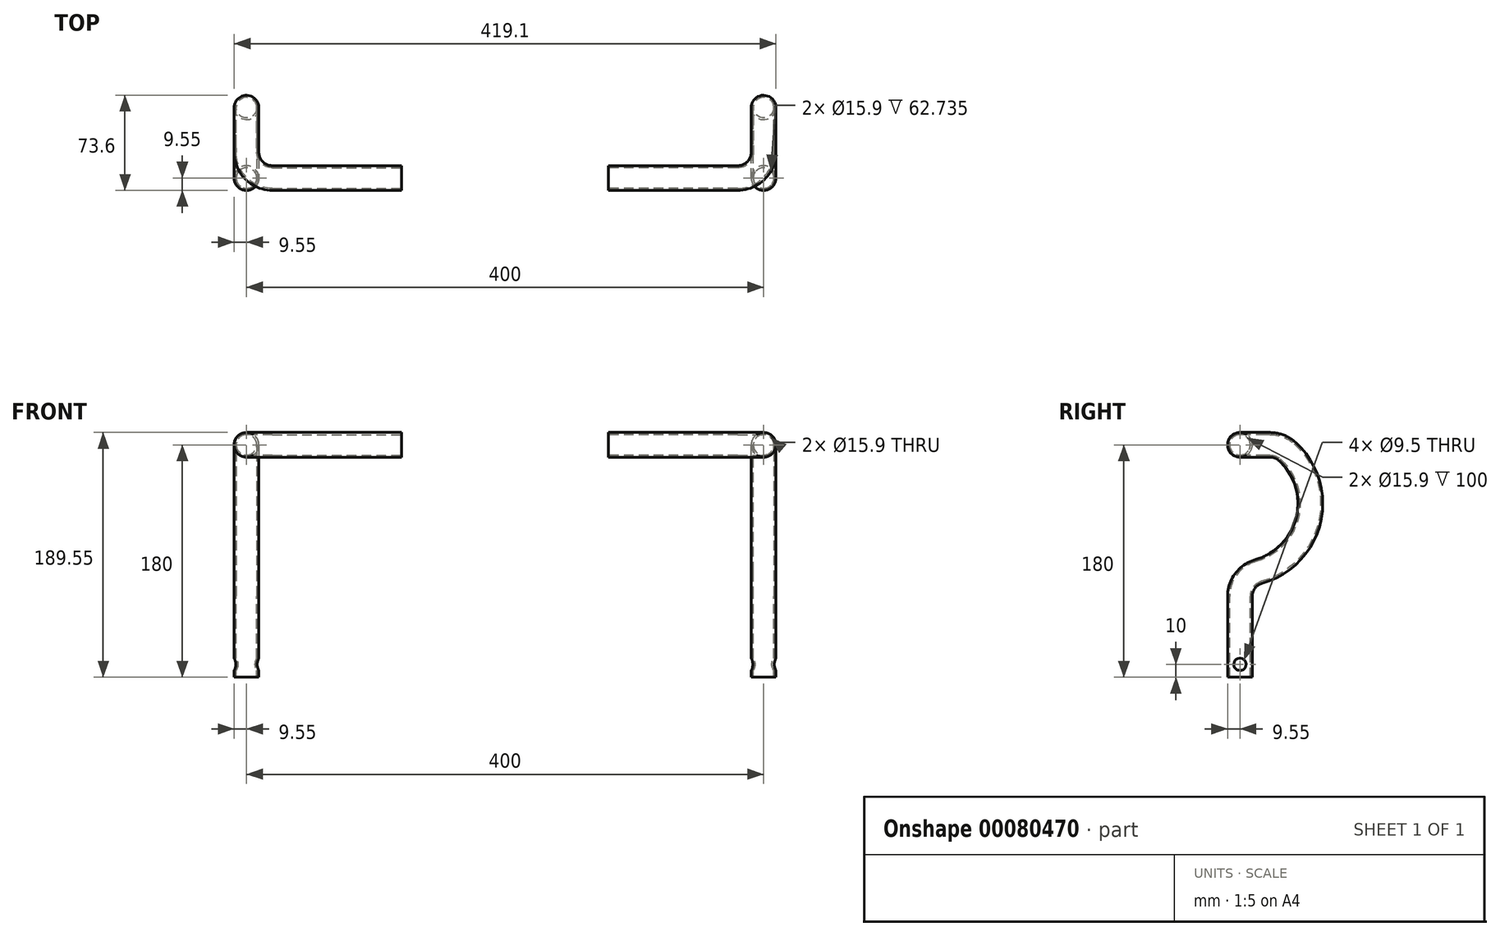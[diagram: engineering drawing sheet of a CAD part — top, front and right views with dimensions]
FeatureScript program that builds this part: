
annotation { "Feature Type Name" : "Feature", "Feature Type Description" : "" }
export const myFeature = defineFeature(function(context is Context, id is Id, definition is map)
    precondition{}
    {
        {
            var Q0;
            Q0=qCreatedBy(makeId("Right.planeOp"),FACE);
            var sketch = newSketch(context, id + "F0", { "sketchPlane" : qUnion([Q0])});
            skLineSegment(sketch, "E0", {"start": v(0, -117.27) * mm, "end": v(0, -180) * mm});
            skLineSegment(sketch, "E1", {"start": v(0, 0) * mm, "end": v(23.24, 0) * mm});
            skArc(sketch, "E2", {"start": v(14.63, -98) * mm, "mid": v(53.02, -58.12) * mm, "end": v(36.7, -5.22) * mm});
            skPoint(sketch, "E3.visualSharp", {"position": v(30, 0) * mm});
            skArc(sketch, "E3.filletArc", {"start": v(36.7, -5.22) * mm, "mid": v(30.46, -1.35) * mm, "end": v(23.24, 0) * mm});
            skPoint(sketch, "E4.visualSharp", {"position": v(0, -100) * mm});
            skArc(sketch, "E4.filletArc", {"start": v(14.63, -98) * mm, "mid": v(4.07, -105.17) * mm, "end": v(0, -117.27) * mm});
            skSolve(sketch);
        }
        {
            var Q0;
            Q0=qCreatedBy(makeId("Top.planeOp"),FACE);
            var sketch = newSketch(context, id + "F1", { "sketchPlane" : qUnion([Q0])});
            skLineSegment(sketch, "E5.0", {"start": v(0, 20) * mm, "end": v(0, 23.24) * mm});
            skLineSegment(sketch, "E6", {"start": v(-20, 0) * mm, "end": v(-120, 0) * mm});
            skPoint(sketch, "E7.visualSharp", {"position": v(0, 0) * mm});
            skArc(sketch, "E7.filletArc", {"start": v(-20, 0) * mm, "mid": v(-5.86, 5.86) * mm, "end": v(0, 20) * mm});
            skSolve(sketch);
        }
        {
            var Q0;
            Q0=sQuery(id+"F0.wireOp",VERTEX,"E0.end");
            var Q1;
            Q1=sQuery(id+"F0.wireOp",EDGE,"E0");
            cPlane(context, id + "F2", {"entities" : qUnion([Q0, Q1]), "cplaneType" : CPlaneType.LINE_POINT, "offset" : 150 * mm, "width" : 150 * mm, "height" : 150 * mm});
        }
        {
            var Q0;
            Q0=qCreatedBy(id+"F2.planeOp",FACE);
            var sketch = newSketch(context, id + "F3", { "sketchPlane" : qUnion([Q0])});
            skPoint(sketch, "E8.0", {"position": v(0, 0) * mm});
            skCircle(sketch, "E9", {"center": v(0, 0) * mm, "radius": 9.55 * mm});
            skCircle(sketch, "E10", {"center": v(0, 0) * mm, "radius": 7.95 * mm});
            skSolve(sketch);
        }
        {
            var Q0;
            Q0=makeQuery(id+"F3.imprint","IMPRINT",FACE,{"disambiguationData":[TD([[makeQuery(id+"F3.imprint","IMPRINT",EDGE,{"derivedFrom":sQuery(id+"F3.wireOp",EDGE,"E9")}),1.0]])]});
            var Q1;
            Q1=sQuery(id+"F0.wireOp",EDGE,"E0");
            var Q2;
            Q2=sQuery(id+"F0.wireOp",EDGE,"E4.filletArc");
            var Q3;
            Q3=sQuery(id+"F0.wireOp",EDGE,"E2");
            var Q4;
            Q4=sQuery(id+"F0.wireOp",EDGE,"E3.filletArc");
            var Q5;
            Q5=sQuery(id+"F1.wireOp",EDGE,"E5.0");
            var Q6;
            Q6=sQuery(id+"F1.wireOp",EDGE,"E7.filletArc");
            var Q7;
            Q7=sQuery(id+"F1.wireOp",EDGE,"E6");
            sweep(context, id + "F4", {"profiles" : qUnion([Q0]), "path" : qUnion([Q1, Q2, Q3, Q4, Q5, Q6, Q7])});
        }
        {
            var Q0;
            Q0=qCreatedBy(makeId("Right.planeOp"),FACE);
            var sketch = newSketch(context, id + "F5", { "sketchPlane" : qUnion([Q0])});
            skPoint(sketch, "E11.0", {"position": v(0, -180) * mm});
            skCircle(sketch, "E12", {"center": v(0, -170) * mm, "radius": 4.75 * mm});
            skSolve(sketch);
        }
        {
            var Q0;
            Q0 = qSketchRegion(id + "F5", true);
            extrude(context, id + "F6", {"entities" : qUnion([Q0]), "operationType" : NewBodyOperationType.REMOVE, "endBound" : BoundingType.THROUGH_ALL, "oppositeDirection" : true, "depth" : 25 * mm, "hasSecondDirection" : true, "secondDirectionBound" : BoundingType.THROUGH_ALL, "secondDirectionOppositeDirection" : false, "secondDirectionDepth" : 25 * mm});
        }
        {
            var Q0;
            Q0=qCreatedBy(makeId("Right.planeOp"),FACE);
            cPlane(context, id + "F7", {"entities" : qUnion([Q0]), "cplaneType" : CPlaneType.OFFSET, "offset" : 200 * mm, "oppositeDirection" : true, "width" : 150 * mm, "height" : 150 * mm});
        }
        {
            var Q0;
            Q0=makeQuery(id+"F4.opSweep","SWEPT_BODY",BODY,{"disambiguationData":[OSD([sQuery(id+"F1.wireOp",EDGE,"E6"),sQuery(id+"F3.wireOp",EDGE,"E9"),sQuery(id+"F3.wireOp",EDGE,"E10")])]});
            var Q1;
            Q1=qCreatedBy(id+"F7.planeOp",FACE);
            mirror(context, id + "F8", {"entities" : qUnion([Q0]), "mirrorPlane" : qUnion([Q1])});
        }
    });
